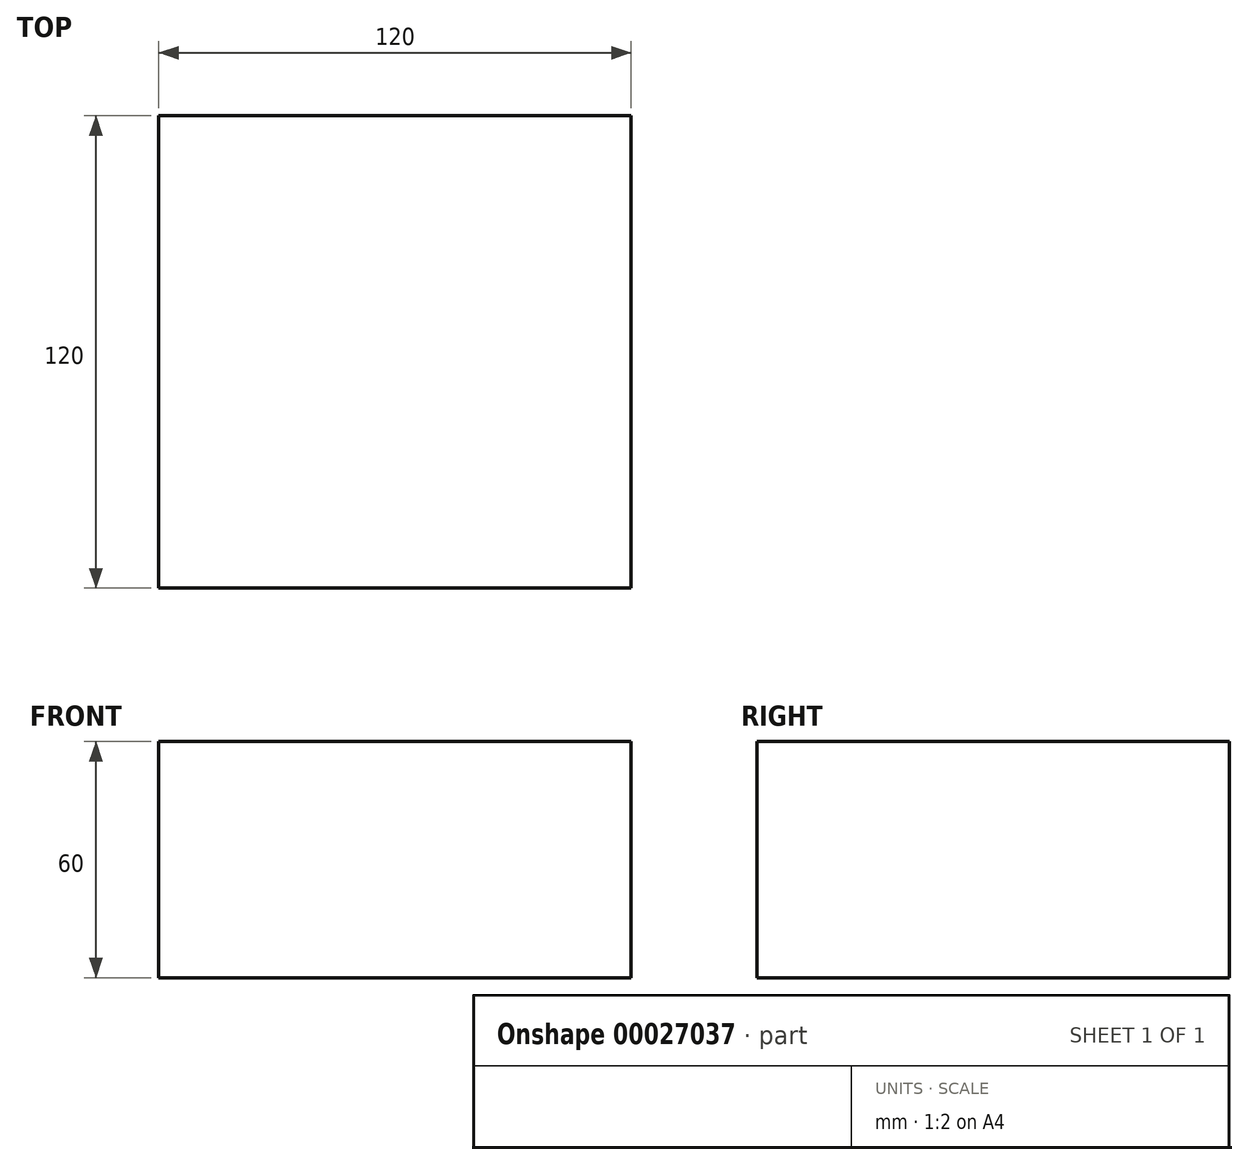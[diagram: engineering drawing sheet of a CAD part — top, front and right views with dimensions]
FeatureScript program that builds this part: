
annotation { "Feature Type Name" : "Feature", "Feature Type Description" : "" }
export const myFeature = defineFeature(function(context is Context, id is Id, definition is map)
    precondition{}
    {
        {
            var Q0;
            Q0=qCreatedBy(makeId("Front.planeOp"),FACE);
            var sketch = newSketch(context, id + "F0", { "sketchPlane" : qUnion([Q0])});
            skLineSegment(sketch, "E0.bottom", {"start": v(0, 0) * mm, "end": v(-120, 0) * mm});
            skLineSegment(sketch, "E0.top", {"start": v(0, -60) * mm, "end": v(-120, -60) * mm});
            skLineSegment(sketch, "E0.left", {"start": v(0, 0) * mm, "end": v(0, -60) * mm});
            skLineSegment(sketch, "E0.right", {"start": v(-120, 0) * mm, "end": v(-120, -60) * mm});
            skSolve(sketch);
        }
        {
            var Q0;
            Q0=makeQuery(id+"F0.imprint","IMPRINT",FACE,{"disambiguationData":[TD([[makeQuery(id+"F0.imprint","IMPRINT",EDGE,{"derivedFrom":sQuery(id+"F0.wireOp",EDGE,"E0.bottom")}),1.0]])]});
            extrude(context, id + "F1", {"entities" : qUnion([Q0]), "oppositeDirection" : true, "depth" : 120 * mm});
        }
    });
